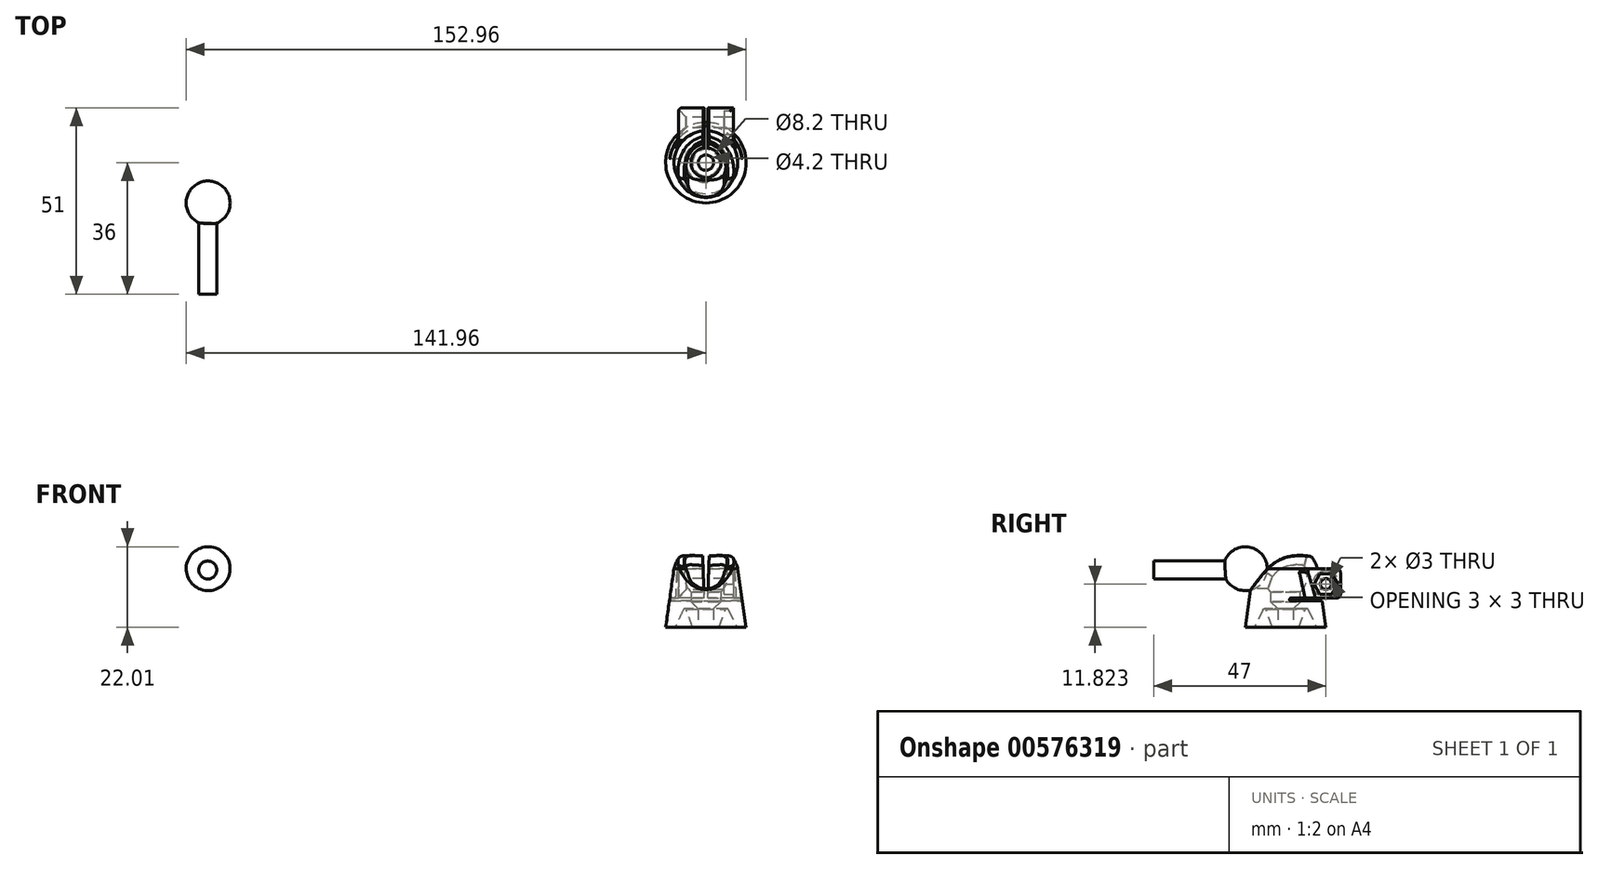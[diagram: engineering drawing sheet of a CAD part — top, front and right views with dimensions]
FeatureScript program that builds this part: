
annotation { "Feature Type Name" : "Feature", "Feature Type Description" : "" }
export const myFeature = defineFeature(function(context is Context, id is Id, definition is map)
    precondition{}
    {
        {
            var Q0;
            Q0=qCreatedBy(makeId("Front.planeOp"),FACE);
            var sketch = newSketch(context, id + "F0", { "sketchPlane" : qUnion([Q0])});
            skArc(sketch, "E0", {"start": v(9, 14.09) * mm, "mid": v(7.61, 18.6) * mm, "end": v(4.13, 21.8) * mm});
            skPoint(sketch, "E1", {"position": v(0, 22.8) * mm});
            skPoint(sketch, "E2", {"position": v(-3.7, 24.25) * mm});
            skLineSegment(sketch, "E3", {"start": v(8.72, 16.04) * mm, "end": v(11, 0) * mm});
            skLineSegment(sketch, "E4", {"start": v(0, -8.26) * mm, "end": v(0, 26.5) * mm});
            skLineSegment(sketch, "E5", {"start": v(11, 0) * mm, "end": v(8.47, 0) * mm});
            skLineSegment(sketch, "E6", {"start": v(6.13, 4.88) * mm, "end": v(8.47, 0) * mm});
            skPoint(sketch, "E7.orphan", {"position": v(5.17, 2) * mm});
            skPoint(sketch, "E8.orphan", {"position": v(2, 0) * mm});
            skPoint(sketch, "E9.visualSharp", {"position": v(5.8, 5.57) * mm});
            skArc(sketch, "E9.filletArc", {"start": v(6.13, 4.88) * mm, "mid": v(5.78, 5.11) * mm, "end": v(5.4, 4.92) * mm});
            skArc(sketch, "E10", {"start": v(4.1, 9.69) * mm, "mid": v(5.92, 14.61) * mm, "end": v(3.13, 19.06) * mm});
            skLineSegment(sketch, "E11", {"start": v(3.13, 19.06) * mm, "end": v(4.13, 21.8) * mm});
            skLineSegment(sketch, "E12", {"start": v(4.1, 7.03) * mm, "end": v(4.1, 9.69) * mm});
            skLineSegment(sketch, "E13", {"start": v(4.1, 7.03) * mm, "end": v(2.1, 5.03) * mm});
            skLineSegment(sketch, "E14", {"start": v(2.1, 0) * mm, "end": v(3.63, 0) * mm});
            skLineSegment(sketch, "E15", {"start": v(3.63, 0) * mm, "end": v(5.4, 4.92) * mm});
            skPoint(sketch, "E16.start.orphan", {"position": v(2.1, 2) * mm});
            skPoint(sketch, "E17.start.orphan", {"position": v(3.63, 2) * mm});
            skLineSegment(sketch, "E18", {"start": v(2.1, 5.03) * mm, "end": v(2.1, 0) * mm});
            skSolve(sketch);
        }
        {
            var Q0;
            {var subQ5=sQuery(id+"F0.wireOp",EDGE,"E5");Q0=makeQuery(id+"F0.imprint","IMPRINT",FACE,{"disambiguationData":[TD([[makeQuery(id+"F0.imprint","IMPRINT",EDGE,{"derivedFrom":subQ5}),-1.0]])]});}
            var Q1;
            Q1=sQuery(id+"F0.wireOp",EDGE,"E4");
            revolve(context, id + "F1", {"entities" : qUnion([Q0]), "axis" : qUnion([Q1]), "revolveType" : RevolveType.FULL});
        }
        {
            var Q0;
            Q0=qCreatedBy(makeId("Front.planeOp"),FACE);
            cPlane(context, id + "F2", {"entities" : qUnion([Q0]), "cplaneType" : CPlaneType.OFFSET, "offset" : 11 * mm, "width" : 150 * mm, "height" : 150 * mm});
        }
        {
            var Q0;
            Q0=qCreatedBy(makeId("Right.planeOp"),FACE);
            var sketch = newSketch(context, id + "F3", { "sketchPlane" : qUnion([Q0])});
            skLineSegment(sketch, "E19", {"start": v(-16.69, 8.57) * mm, "end": v(-19.5, 6.94) * mm});
            skLineSegment(sketch, "E20", {"start": v(-19.5, 6.94) * mm, "end": v(-22.83, 12.7) * mm});
            skLineSegment(sketch, "E21", {"start": v(-22.83, 12.7) * mm, "end": v(-20.02, 14.33) * mm});
            skLineSegment(sketch, "E22", {"start": v(-20.02, 14.33) * mm, "end": v(-16.69, 8.57) * mm});
            skSolve(sketch);
        }
        {
            var Q0;
            Q0=sQuery(id+"F3.wireOp",EDGE,"E20");
            cPlane(context, id + "F4", {"entities" : qUnion([Q0]), "cplaneType" : CPlaneType.LINE_ANGLE, "offset" : 25 * mm, "angle" : 90 * degree, "width" : 150 * mm, "height" : 150 * mm});
        }
        {
            var Q0;
            Q0=qCreatedBy(id+"F4.planeOp",FACE);
            var sketch = newSketch(context, id + "F5", { "sketchPlane" : qUnion([Q0])});
            skCircle(sketch, "E23", {"center": v(0, 21.76) * mm, "radius": 7.75 * mm});
            skSolve(sketch);
        }
        {
            var Q0;
            Q0=qCreatedBy(makeId("Front.planeOp"),FACE);
            cPlane(context, id + "F6", {"entities" : qUnion([Q0]), "cplaneType" : CPlaneType.OFFSET, "offset" : 15 * mm, "oppositeDirection" : true, "width" : 150 * mm, "height" : 150 * mm});
        }
        {
            var Q0;
            Q0=qCreatedBy(id+"F6.planeOp",FACE);
            var sketch = newSketch(context, id + "F7", { "sketchPlane" : qUnion([Q0])});
            skLineSegment(sketch, "E24", {"start": v(1, 23) * mm, "end": v(-1, 23) * mm});
            skLineSegment(sketch, "E25", {"start": v(1, 23) * mm, "end": v(0.5, 8) * mm});
            skLineSegment(sketch, "E26", {"start": v(-1, 23) * mm, "end": v(-0.5, 8) * mm});
            skLineSegment(sketch, "E27", {"start": v(0.5, 8) * mm, "end": v(-0.5, 8) * mm});
            skSolve(sketch);
        }
        {
            var Q0;
            Q0=qCreatedBy(id+"F6.planeOp",FACE);
            var sketch = newSketch(context, id + "F8", { "sketchPlane" : qUnion([Q0])});
            skLineSegment(sketch, "E28.bottom", {"start": v(7.5, 16) * mm, "end": v(-7.5, 16) * mm});
            skLineSegment(sketch, "E28.top", {"start": v(7.5, 8) * mm, "end": v(-7.5, 8) * mm});
            skLineSegment(sketch, "E28.left", {"start": v(7.5, 16) * mm, "end": v(7.5, 8) * mm});
            skLineSegment(sketch, "E28.right", {"start": v(-7.5, 16) * mm, "end": v(-7.5, 8) * mm});
            skSolve(sketch);
        }
        {
            var Q0;
            Q0=makeQuery(id+"F8.imprint","IMPRINT",FACE,{"disambiguationData":[TD([[makeQuery(id+"F8.imprint","IMPRINT",EDGE,{"derivedFrom":sQuery(id+"F8.wireOp",EDGE,"E28.bottom")}),1.0]])]});
            extrude(context, id + "F9", {"entities" : qUnion([Q0]), "operationType" : NewBodyOperationType.ADD, "depth" : 9 * mm, "offsetDistance" : 25 * mm});
        }
        {
            var Q0;
            Q0=makeQuery(id+"F5.imprint","IMPRINT",FACE,{"disambiguationData":[TD([[makeQuery(id+"F5.imprint","IMPRINT",EDGE,{"derivedFrom":sQuery(id+"F5.wireOp",EDGE,"E23")}),1.0]])]});
            extrude(context, id + "F10", {"entities" : qUnion([Q0]), "operationType" : NewBodyOperationType.REMOVE, "depth" : 56 * mm, "offsetDistance" : 25 * mm});
        }
        {
            var Q0;
            Q0=makeQuery(id+"F7.imprint","IMPRINT",FACE,{"disambiguationData":[TD([[makeQuery(id+"F7.imprint","IMPRINT",EDGE,{"derivedFrom":sQuery(id+"F7.wireOp",EDGE,"E24")}),1.0]])]});
            extrude(context, id + "F11", {"entities" : qUnion([Q0]), "operationType" : NewBodyOperationType.REMOVE, "depth" : 14.3 * mm, "offsetDistance" : 25 * mm});
        }
        {
            var Q0;
            {var subQ0=sQuery(id+"F8.wireOp",EDGE,"E28.bottom");var subQ1=sQuery(id+"F8.wireOp",EDGE,"E28.right");Q0=makeQuery(id+"F9.boolean.opBoolean","SPLIT",FACE,{"disambiguationData":[TD([makeQuery(id+"F9.opExtrude","SWEPT_FACE",FACE,{"disambiguationData":[OSD([subQ1])]})])],"derivedFrom":makeQuery(id+"F9.opExtrude","CAP_FACE",FACE,{"disambiguationData":[OSD([subQ0,sQuery(id+"F8.wireOp",EDGE,"E28.top"),sQuery(id+"F8.wireOp",EDGE,"E28.left"),subQ1])],"isStart":false})});}
            extrude(context, id + "F12", {"entities" : qUnion([Q0]), "operationType" : NewBodyOperationType.ADD, "depth" : 2 * mm, "offsetDistance" : 25 * mm});
        }
        {
            var Q0;
            {var subQ0=sQuery(id+"F8.wireOp",EDGE,"E28.left");var subQ1=sQuery(id+"F8.wireOp",EDGE,"E28.bottom");Q0=makeQuery(id+"F9.boolean.opBoolean","SPLIT",FACE,{"disambiguationData":[TD([makeQuery(id+"F9.opExtrude","SWEPT_FACE",FACE,{"disambiguationData":[OSD([subQ0])]})])],"derivedFrom":makeQuery(id+"F9.opExtrude","CAP_FACE",FACE,{"disambiguationData":[OSD([subQ1,sQuery(id+"F8.wireOp",EDGE,"E28.top"),subQ0,sQuery(id+"F8.wireOp",EDGE,"E28.right")])],"isStart":false})});}
            extrude(context, id + "F13", {"entities" : qUnion([Q0]), "operationType" : NewBodyOperationType.ADD, "depth" : 2 * mm, "offsetDistance" : 25 * mm});
        }
        {
            var Q0;
            Q0=makeQuery(id+"F12.boolean.opBoolean","INTERSECT",EDGE,{"derivedFrom":[makeQuery(id+"F1.opRevolve","SWEPT_FACE",FACE,{"disambiguationData":[OSD([sQuery(id+"F0.wireOp",EDGE,"E3")])]}),makeQuery(id+"F12.opExtrude","SWEPT_FACE",FACE,{"disambiguationData":[OSD([sQuery(id+"F8.wireOp",EDGE,"E28.right")])]})]});
            var Q1;
            Q1=makeQuery(id+"F13.boolean.opBoolean","INTERSECT",EDGE,{"derivedFrom":[makeQuery(id+"F1.opRevolve","SWEPT_FACE",FACE,{"disambiguationData":[OSD([sQuery(id+"F0.wireOp",EDGE,"E3")])]}),makeQuery(id+"F13.opExtrude","SWEPT_FACE",FACE,{"disambiguationData":[OSD([sQuery(id+"F8.wireOp",EDGE,"E28.left")])]})]});
            fillet(context, id + "F14", {"entities" : qUnion([Q0, Q1]), "radius" : 5 * mm, "tangentPropagation" : true, "allowEdgeOverflow" : false});
        }
        {
            var Q0;
            Q0=makeQuery(id+"F9.opExtrude","CAP_EDGE",EDGE,{"disambiguationData":[OSD([sQuery(id+"F8.wireOp",EDGE,"E28.right")])],"isStart":true});
            var Q1;
            {var subQ0=sQuery(id+"F8.wireOp",EDGE,"E28.left");var subQ1=sQuery(id+"F8.wireOp",EDGE,"E28.top");Q1=makeQuery(id+"F11.boolean.opBoolean","SPLIT",EDGE,{"disambiguationData":[TD([makeQuery(id+"F9.opExtrude","SWEPT_FACE",FACE,{"disambiguationData":[OSD([subQ0])]})])],"derivedFrom":makeQuery(id+"F9.opExtrude","CAP_EDGE",EDGE,{"disambiguationData":[OSD([subQ1])],"isStart":true})});}
            var Q2;
            {var subQ0=sQuery(id+"F8.wireOp",EDGE,"E28.right");var subQ1=sQuery(id+"F8.wireOp",EDGE,"E28.top");Q2=makeQuery(id+"F11.boolean.opBoolean","SPLIT",EDGE,{"disambiguationData":[TD([makeQuery(id+"F9.opExtrude","SWEPT_FACE",FACE,{"disambiguationData":[OSD([subQ0])]})])],"derivedFrom":makeQuery(id+"F9.opExtrude","CAP_EDGE",EDGE,{"disambiguationData":[OSD([subQ1])],"isStart":true})});}
            var Q3;
            {var subQ0=sQuery(id+"F8.wireOp",EDGE,"E28.right");var subQ1=makeQuery(id+"F9.opExtrude","SWEPT_FACE",FACE,{"disambiguationData":[OSD([subQ0])]});var subQ2=makeQuery(id+"F9.opExtrude","SWEPT_FACE",FACE,{"disambiguationData":[OSD([sQuery(id+"F8.wireOp",EDGE,"E28.top")])]});var subQ3=makeQuery(id+"F1.opRevolve","SWEPT_FACE",FACE,{"disambiguationData":[OSD([sQuery(id+"F0.wireOp",EDGE,"E3")])]});Q3=makeQuery(id+"F14.opFillet","BLEND_EDGE",EDGE,{"blendedFrom":[makeQuery(id+"F11.boolean.opBoolean","SPLIT",EDGE,{"disambiguationData":[topologyDisambiguationEdgeConnected([subQ3,subQ2]),TD([subQ1])],"derivedFrom":makeQuery(id+"F9.boolean.opBoolean","INTERSECT",EDGE,{"derivedFrom":[subQ3,subQ2]})}),makeQuery(id+"F12.boolean.opBoolean","MERGE",FACE,{"derivedFrom":[subQ1,makeQuery(id+"F12.opExtrude","SWEPT_FACE",FACE,{"disambiguationData":[OSD([subQ0])]})]})],"blendedInto":[makeQuery(id+"F12.boolean.opBoolean","MERGE",FACE,{"derivedFrom":[subQ1,makeQuery(id+"F12.opExtrude","SWEPT_FACE",FACE,{"disambiguationData":[OSD([subQ0])]})]})]});}
            var Q4;
            {var subQ0=sQuery(id+"F8.wireOp",EDGE,"E28.left");var subQ1=makeQuery(id+"F9.opExtrude","SWEPT_FACE",FACE,{"disambiguationData":[OSD([subQ0])]});var subQ2=makeQuery(id+"F1.opRevolve","SWEPT_FACE",FACE,{"disambiguationData":[OSD([sQuery(id+"F0.wireOp",EDGE,"E3")])]});var subQ3=makeQuery(id+"F9.opExtrude","SWEPT_FACE",FACE,{"disambiguationData":[OSD([sQuery(id+"F8.wireOp",EDGE,"E28.top")])]});Q4=makeQuery(id+"F14.opFillet","BLEND_EDGE",EDGE,{"blendedFrom":[makeQuery(id+"F11.boolean.opBoolean","SPLIT",EDGE,{"disambiguationData":[topologyDisambiguationEdgeConnected([subQ2,subQ3]),TD([subQ1])],"derivedFrom":makeQuery(id+"F9.boolean.opBoolean","INTERSECT",EDGE,{"derivedFrom":[subQ2,subQ3]})}),makeQuery(id+"F13.boolean.opBoolean","MERGE",FACE,{"derivedFrom":[subQ1,makeQuery(id+"F13.opExtrude","SWEPT_FACE",FACE,{"disambiguationData":[OSD([subQ0])]})]})],"blendedInto":[makeQuery(id+"F13.boolean.opBoolean","MERGE",FACE,{"derivedFrom":[subQ1,makeQuery(id+"F13.opExtrude","SWEPT_FACE",FACE,{"disambiguationData":[OSD([subQ0])]})]})]});}
            var Q5;
            {var subQ0=sQuery(id+"F8.wireOp",EDGE,"E28.bottom");var subQ1=sQuery(id+"F8.wireOp",EDGE,"E28.left");Q5=makeQuery(id+"F11.boolean.opBoolean","SPLIT",EDGE,{"disambiguationData":[TD([makeQuery(id+"F9.opExtrude","SWEPT_FACE",FACE,{"disambiguationData":[OSD([subQ1])]})])],"derivedFrom":makeQuery(id+"F9.opExtrude","CAP_EDGE",EDGE,{"disambiguationData":[OSD([subQ0])],"isStart":true})});}
            var Q6;
            {var subQ0=sQuery(id+"F8.wireOp",EDGE,"E28.bottom");var subQ1=sQuery(id+"F8.wireOp",EDGE,"E28.right");Q6=makeQuery(id+"F11.boolean.opBoolean","SPLIT",EDGE,{"disambiguationData":[TD([makeQuery(id+"F9.opExtrude","SWEPT_FACE",FACE,{"disambiguationData":[OSD([subQ1])]})])],"derivedFrom":makeQuery(id+"F9.opExtrude","CAP_EDGE",EDGE,{"disambiguationData":[OSD([subQ0])],"isStart":true})});}
            var Q7;
            {var subQ0=sQuery(id+"F8.wireOp",EDGE,"E28.right");var subQ1=sQuery(id+"F8.wireOp",EDGE,"E28.bottom");Q7=makeQuery(id+"F12.boolean.opBoolean","MERGE",EDGE,{"derivedFrom":[makeQuery(id+"F9.opExtrude","SWEPT_EDGE",EDGE,{"disambiguationData":[OSD([subQ1,subQ0])]}),makeQuery(id+"F12.opExtrude","SWEPT_EDGE",EDGE,{"disambiguationData":[OSD([subQ1,subQ0])]})]});}
            var Q8;
            {var subQ0=sQuery(id+"F8.wireOp",EDGE,"E28.left");var subQ1=sQuery(id+"F8.wireOp",EDGE,"E28.bottom");Q8=makeQuery(id+"F13.boolean.opBoolean","MERGE",EDGE,{"derivedFrom":[makeQuery(id+"F9.opExtrude","SWEPT_EDGE",EDGE,{"disambiguationData":[OSD([subQ1,subQ0])]}),makeQuery(id+"F13.opExtrude","SWEPT_EDGE",EDGE,{"disambiguationData":[OSD([subQ1,subQ0])]})]});}
            fillet(context, id + "F15", {"entities" : qUnion([Q0, Q1, Q2, Q3, Q4, Q5, Q6, Q7, Q8]), "radius" : 1 * mm, "tangentPropagation" : true, "allowEdgeOverflow" : false});
        }
        {
            var Q0;
            {var subQ0=sQuery(id+"F8.wireOp",EDGE,"E28.bottom");var subQ1=sQuery(id+"F8.wireOp",EDGE,"E28.right");var subQ2=sQuery(id+"F8.wireOp",EDGE,"E28.top");Q0=makeQuery(id+"F11.boolean.opBoolean","SPLIT",FACE,{"disambiguationData":[TD([makeQuery(id+"F9.opExtrude","SWEPT_FACE",FACE,{"disambiguationData":[OSD([subQ1])]})])],"derivedFrom":makeQuery(id+"F9.opExtrude","CAP_FACE",FACE,{"disambiguationData":[OSD([subQ0,subQ2,sQuery(id+"F8.wireOp",EDGE,"E28.left"),subQ1])],"isStart":true})});}
            cPlane(context, id + "F16", {"entities" : qUnion([Q0]), "cplaneType" : CPlaneType.OFFSET, "offset" : 4 * mm, "oppositeDirection" : true, "width" : 150 * mm, "height" : 150 * mm});
        }
        {
            var Q0;
            Q0=qCreatedBy(id+"F16.planeOp",FACE);
            var sketch = newSketch(context, id + "F17", { "sketchPlane" : qUnion([Q0])});
            skLineSegment(sketch, "E29", {"start": v(-11.4, 11.82) * mm, "end": v(10.09, 11.82) * mm});
            skLineSegment(sketch, "E30", {"start": v(5.39, 13.32) * mm, "end": v(-9.61, 13.32) * mm});
            skLineSegment(sketch, "E31", {"start": v(5.39, 13.32) * mm, "end": v(8.53, 16.47) * mm});
            skLineSegment(sketch, "E32", {"start": v(8.53, 16.47) * mm, "end": v(8.53, 11.82) * mm});
            skLineSegment(sketch, "E33", {"start": v(-9.61, 13.32) * mm, "end": v(-9.61, 11.82) * mm});
            skSolve(sketch);
        }
        {
            var Q0;
            Q0=makeQuery(id+"F17.imprint","IMPRINT",FACE,{"disambiguationData":[TD([[makeQuery(id+"F17.imprint","IMPRINT",EDGE,{"derivedFrom":sQuery(id+"F17.wireOp",EDGE,"E30")}),1.0]])]});
            var Q1;
            Q1=sQuery(id+"F17.wireOp",EDGE,"E29");
            revolve(context, id + "F18", {"operationType" : NewBodyOperationType.REMOVE, "entities" : qUnion([Q0]), "axis" : qUnion([Q1]), "revolveType" : RevolveType.FULL, "oppositeDirection" : true});
        }
        {
            var Q0;
            Q0=qCreatedBy(id+"F6.planeOp",FACE);
            var sketch = newSketch(context, id + "F19", { "sketchPlane" : qUnion([Q0])});
            skLineSegment(sketch, "E34.bottom", {"start": v(15, 8) * mm, "end": v(-15, 8) * mm});
            skLineSegment(sketch, "E34.top", {"start": v(15, 7.2) * mm, "end": v(-15, 7.2) * mm});
            skLineSegment(sketch, "E34.left", {"start": v(15, 8) * mm, "end": v(15, 7.2) * mm});
            skLineSegment(sketch, "E34.right", {"start": v(-15, 8) * mm, "end": v(-15, 7.2) * mm});
            skSolve(sketch);
        }
        {
            var Q0;
            Q0=makeQuery(id+"F19.imprint","IMPRINT",FACE,{"disambiguationData":[TD([[makeQuery(id+"F19.imprint","IMPRINT",EDGE,{"derivedFrom":sQuery(id+"F19.wireOp",EDGE,"E34.bottom")}),1.0]])]});
            extrude(context, id + "F20", {"entities" : qUnion([Q0]), "operationType" : NewBodyOperationType.REMOVE, "depth" : 13.9 * mm, "offsetDistance" : 25 * mm});
        }
        {
            var Q0;
            {var subQ0=sQuery(id+"F8.wireOp",EDGE,"E28.left");Q0=makeQuery(id+"F13.boolean.opBoolean","MERGE",FACE,{"derivedFrom":[makeQuery(id+"F9.opExtrude","SWEPT_FACE",FACE,{"disambiguationData":[OSD([subQ0])]}),makeQuery(id+"F13.opExtrude","SWEPT_FACE",FACE,{"disambiguationData":[OSD([subQ0])]})]});}
            var sketch = newSketch(context, id + "F21", { "sketchPlane" : qUnion([Q0])});
            skCircle(sketch, "E35.cCircle", {"center": v(11, 11.82) * mm, "radius": 2.8 * mm, "construction": true});
            skLineSegment(sketch, "E35.0", {"start": v(9.38, 14.62) * mm, "end": v(12.62, 14.62) * mm});
            skLineSegment(sketch, "E35.1", {"start": v(12.62, 14.62) * mm, "end": v(14.23, 11.82) * mm});
            skLineSegment(sketch, "E35.2", {"start": v(14.23, 11.82) * mm, "end": v(12.62, 9.02) * mm});
            skLineSegment(sketch, "E35.3", {"start": v(12.62, 9.02) * mm, "end": v(9.38, 9.02) * mm});
            skLineSegment(sketch, "E35.4", {"start": v(9.38, 9.02) * mm, "end": v(7.77, 11.82) * mm});
            skLineSegment(sketch, "E35.5", {"start": v(7.77, 11.82) * mm, "end": v(9.38, 14.62) * mm});
            skPoint(sketch, "E35.0.midPoint", {"position": v(11, 14.62) * mm});
            skSolve(sketch);
        }
        {
            var Q0;
            {var subQ7=sQuery(id+"F21.wireOp",EDGE,"E35.0");Q0=makeQuery(id+"F21.imprint","IMPRINT",FACE,{"disambiguationData":[TD([[makeQuery(id+"F21.imprint","IMPRINT",EDGE,{"derivedFrom":subQ7}),-1.0]])]});}
            extrude(context, id + "F22", {"entities" : qUnion([Q0]), "operationType" : NewBodyOperationType.REMOVE, "oppositeDirection" : true, "depth" : 2.5 * mm, "offsetDistance" : 25 * mm});
        }
        {
            var Q0;
            Q0=qCreatedBy(id+"F2.planeOp",FACE);
            var sketch = newSketch(context, id + "F23", { "sketchPlane" : qUnion([Q0])});
            skArc(sketch, "E36", {"start": v(-136.8, 10.06) * mm, "mid": v(-130.02, 15.17) * mm, "end": v(-135.12, 21.95) * mm});
            skLineSegment(sketch, "E37", {"start": v(-134.23, 28.26) * mm, "end": v(-138.22, 0) * mm});
            skSolve(sketch);
        }
        {
            var Q0;
            {var subQ0=makeQuery(id+"F1.opRevolve","SWEPT_FACE",FACE,{"disambiguationData":[OSD([sQuery(id+"F0.wireOp",EDGE,"E0")])]});var subQ1=makeQuery(id+"F10.opExtrude","SWEPT_FACE",FACE,{"disambiguationData":[OSD([sQuery(id+"F5.wireOp",EDGE,"E23")])]});Q0=makeQuery(id+"F11.boolean.opBoolean","SPLIT",EDGE,{"disambiguationData":[TD([makeQuery(id+"F11.opExtrude","SWEPT_FACE",FACE,{"disambiguationData":[OSD([sQuery(id+"F7.wireOp",EDGE,"E26")])]})])],"derivedFrom":makeQuery(id+"F10.boolean.opBoolean","INTERSECT",EDGE,{"derivedFrom":[subQ0,subQ1]})});}
            var Q1;
            Q1=makeQuery(id+"F10.boolean.opBoolean","INTERSECT",EDGE,{"derivedFrom":[makeQuery(id+"F1.opRevolve","SWEPT_FACE",FACE,{"disambiguationData":[OSD([sQuery(id+"F0.wireOp",EDGE,"E3")])]}),makeQuery(id+"F10.opExtrude","SWEPT_FACE",FACE,{"disambiguationData":[OSD([sQuery(id+"F5.wireOp",EDGE,"E23")])]})]});
            var Q2;
            {var subQ0=makeQuery(id+"F1.opRevolve","SWEPT_FACE",FACE,{"disambiguationData":[OSD([sQuery(id+"F0.wireOp",EDGE,"E0")])]});var subQ1=makeQuery(id+"F10.opExtrude","SWEPT_FACE",FACE,{"disambiguationData":[OSD([sQuery(id+"F5.wireOp",EDGE,"E23")])]});Q2=makeQuery(id+"F11.boolean.opBoolean","SPLIT",EDGE,{"disambiguationData":[TD([makeQuery(id+"F11.opExtrude","SWEPT_FACE",FACE,{"disambiguationData":[OSD([sQuery(id+"F7.wireOp",EDGE,"E25")])]})])],"derivedFrom":makeQuery(id+"F10.boolean.opBoolean","INTERSECT",EDGE,{"derivedFrom":[subQ0,subQ1]})});}
            chamfer(context, id + "F24", {"entities" : qUnion([Q0, Q1, Q2]), "width" : 1 * mm, "tangentPropagation" : true});
        }
        {
            var Q0;
            {var subQ0=sQuery(id+"F23.wireOp",EDGE,"E36");Q0=makeQuery(id+"F23.imprint","IMPRINT",FACE,{"disambiguationData":[TD([[makeQuery(id+"F23.imprint","IMPRINT",EDGE,{"derivedFrom":subQ0}),1.0]])]});}
            var Q1;
            Q1=sQuery(id+"F23.wireOp",EDGE,"E37");
            revolve(context, id + "F25", {"entities" : qUnion([Q0]), "axis" : qUnion([Q1]), "revolveType" : RevolveType.FULL});
        }
        {
            var Q0;
            Q0=qCreatedBy(id+"F2.planeOp",FACE);
            var sketch = newSketch(context, id + "F26", { "sketchPlane" : qUnion([Q0])});
            skCircle(sketch, "E38", {"center": v(-136.06, 15.65) * mm, "radius": 2.46 * mm});
            skSolve(sketch);
        }
        {
            var Q0;
            Q0 = qSketchRegion(id + "F26", true);
            extrude(context, id + "F27", {"entities" : qUnion([Q0]), "operationType" : NewBodyOperationType.ADD, "depth" : 25 * mm, "offsetDistance" : 25 * mm});
        }
        {
            var Q0;
            Q0=makeQuery(id+"F10.boolean.opBoolean","INTERSECT",EDGE,{"derivedFrom":[makeQuery(id+"F1.opRevolve","SWEPT_FACE",FACE,{"disambiguationData":[OSD([sQuery(id+"F0.wireOp",EDGE,"E10")])]}),makeQuery(id+"F10.opExtrude","SWEPT_FACE",FACE,{"disambiguationData":[OSD([sQuery(id+"F5.wireOp",EDGE,"E23")])]})]});
            chamfer(context, id + "F28", {"entities" : qUnion([Q0]), "width" : 2 * mm, "tangentPropagation" : true});
        }
        {
            var Q0;
            Q0=makeQuery(id+"F20.boolean.opBoolean","COPY",EDGE,{"disambiguationData":[OD(1.0)],"derivedFrom":makeQuery(id+"F20.opExtrude","CAP_EDGE",EDGE,{"disambiguationData":[OSD([sQuery(id+"F19.wireOp",EDGE,"E34.top")])],"isStart":false})});
            var Q1;
            Q1=makeQuery(id+"F20.boolean.opBoolean","COPY",EDGE,{"disambiguationData":[OD(1.0)],"derivedFrom":makeQuery(id+"F20.opExtrude","CAP_EDGE",EDGE,{"disambiguationData":[OSD([sQuery(id+"F19.wireOp",EDGE,"E34.bottom")])],"isStart":false})});
            var Q2;
            Q2=makeQuery(id+"F20.boolean.opBoolean","COPY",EDGE,{"disambiguationData":[OD(0.0)],"derivedFrom":makeQuery(id+"F20.opExtrude","CAP_EDGE",EDGE,{"disambiguationData":[OSD([sQuery(id+"F19.wireOp",EDGE,"E34.top")])],"isStart":false})});
            var Q3;
            Q3=makeQuery(id+"F20.boolean.opBoolean","COPY",EDGE,{"disambiguationData":[OD(0.0)],"derivedFrom":makeQuery(id+"F20.opExtrude","CAP_EDGE",EDGE,{"disambiguationData":[OSD([sQuery(id+"F19.wireOp",EDGE,"E34.bottom")])],"isStart":false})});
            fillet(context, id + "F29", {"entities" : qUnion([Q0, Q1, Q2, Q3]), "radius" : 0.4 * mm, "tangentPropagation" : true, "allowEdgeOverflow" : false});
        }
        {
            var Q0;
            Q0=qCreatedBy(id+"F2.planeOp",FACE);
            var sketch = newSketch(context, id + "F30", { "sketchPlane" : qUnion([Q0])});
            skCircle(sketch, "E39", {"center": v(0, 15.48) * mm, "radius": 5 * mm});
            skSolve(sketch);
        }
        {
            var Q0;
            Q0=makeQuery(id+"F30.imprint","IMPRINT",FACE,{"disambiguationData":[TD([[makeQuery(id+"F30.imprint","IMPRINT",EDGE,{"derivedFrom":sQuery(id+"F30.wireOp",EDGE,"E39")}),1.0]])]});
            extrude(context, id + "F31", {"entities" : qUnion([Q0]), "operationType" : NewBodyOperationType.REMOVE, "oppositeDirection" : true, "depth" : 8.2 * mm, "offsetDistance" : 25 * mm});
        }
    });
